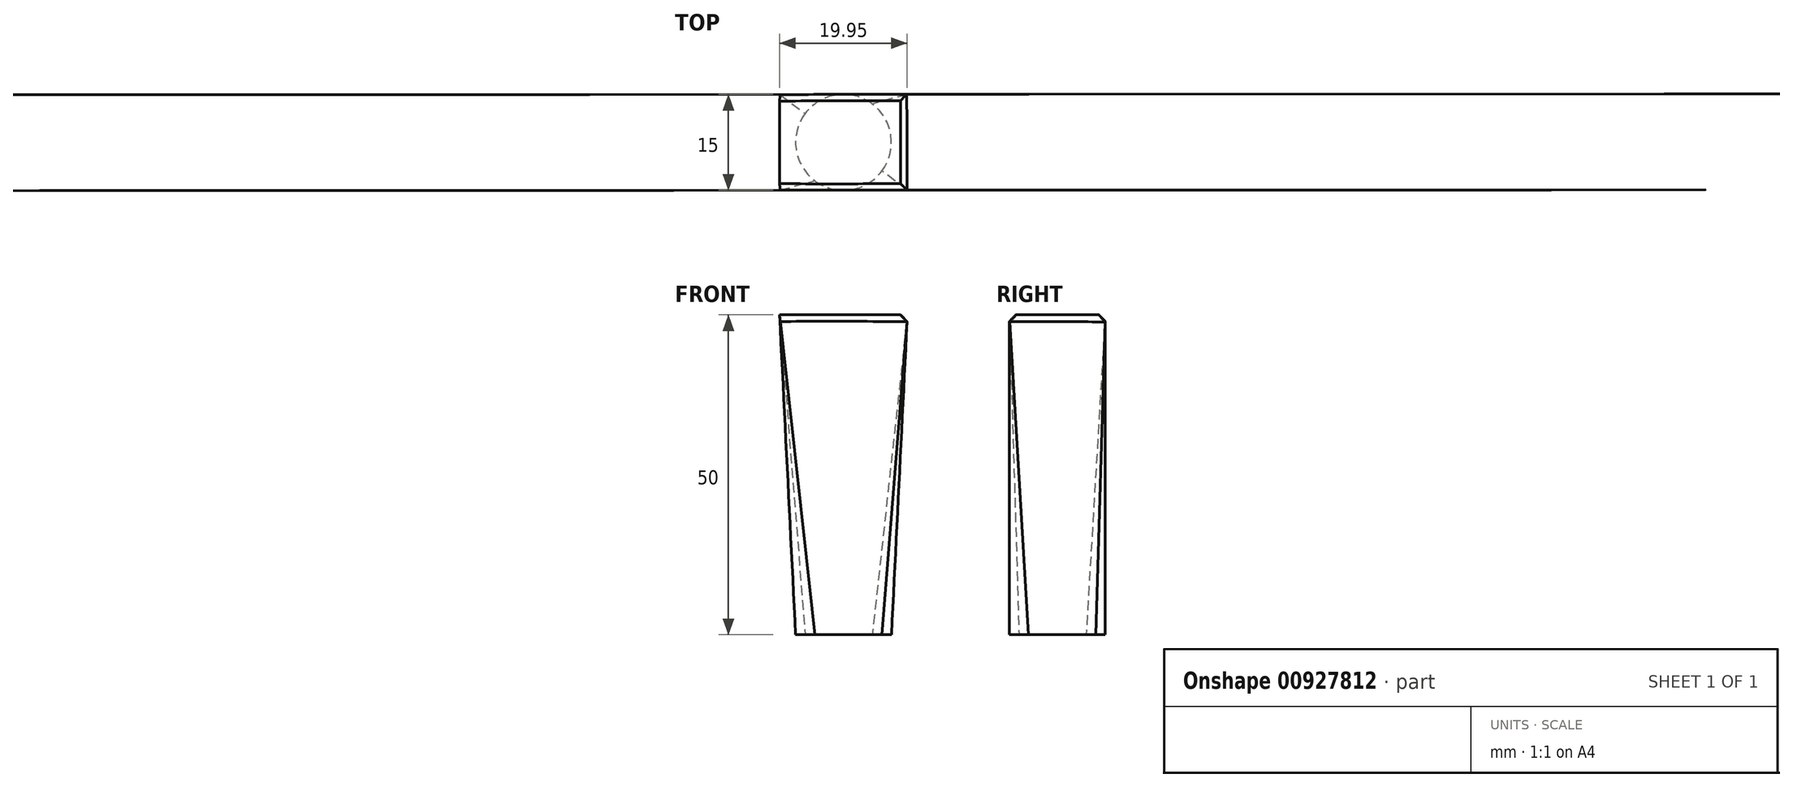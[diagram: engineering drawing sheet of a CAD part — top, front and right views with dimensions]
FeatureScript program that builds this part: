
annotation { "Feature Type Name" : "Feature", "Feature Type Description" : "" }
export const myFeature = defineFeature(function(context is Context, id is Id, definition is map)
    precondition{}
    {
        {
            var Q0;
            Q0=qCreatedBy(makeId("Top.planeOp"),FACE);
            var sketch = newSketch(context, id + "F0", { "sketchPlane" : qUnion([Q0])});
            skCircle(sketch, "E0", {"center": v(0, 0) * mm, "radius": 7.5 * mm});
            skSolve(sketch);
        }
        {
            var Q0;
            Q0=qCreatedBy(makeId("Top.planeOp"),FACE);
            cPlane(context, id + "F1", {"entities" : qUnion([Q0]), "cplaneType" : CPlaneType.OFFSET, "offset" : 50 * mm, "width" : 150 * mm, "height" : 150 * mm});
        }
        {
            var Q0;
            Q0=qCreatedBy(id+"F1.planeOp",FACE);
            var sketch = newSketch(context, id + "F2", { "sketchPlane" : qUnion([Q0])});
            skLineSegment(sketch, "E1.bottom", {"start": v(-10, 7.5) * mm, "end": v(10, 7.5) * mm});
            skLineSegment(sketch, "E1.top", {"start": v(-10, -7.5) * mm, "end": v(10, -7.5) * mm});
            skLineSegment(sketch, "E1.left", {"start": v(-10, 7.5) * mm, "end": v(-10, -7.5) * mm});
            skLineSegment(sketch, "E1.right", {"start": v(10, 7.5) * mm, "end": v(10, -7.5) * mm});
            skPoint(sketch, "E1.middle", {"position": v(0, 0) * mm});
            skSolve(sketch);
        }
        {
            var Q0;
            Q0=makeQuery(id+"F2.imprint","IMPRINT",FACE,{"disambiguationData":[TD([[makeQuery(id+"F2.imprint","IMPRINT",EDGE,{"derivedFrom":sQuery(id+"F2.wireOp",EDGE,"E1.bottom")}),-1.0]])]});
            var Q1;
            Q1=makeQuery(id+"F0.imprint","IMPRINT",FACE,{"disambiguationData":[TD([[makeQuery(id+"F0.imprint","IMPRINT",EDGE,{"derivedFrom":sQuery(id+"F0.wireOp",EDGE,"E0")}),1.0]])]});
            loft(context, id + "F3", {"sheetProfilesArray" : [{ "sheetProfileEntities" : qUnion([Q0]) }, { "sheetProfileEntities" : qUnion([Q1]) }]});
        }
        {
            var Q0;
            Q0=makeQuery(id+"F3.opLoft","MID_CAP_EDGE",EDGE,{"disambiguationData":[OSD([sQuery(id+"F2.wireOp",EDGE,"E1.top"),sQuery(id+"F2.wireOp",EDGE,"E1.left"),sQuery(id+"F2.wireOp",EDGE,"E1.right")])],"capPos":0.0});
            var Q1;
            Q1=makeQuery(id+"F3.opLoft","MID_CAP_EDGE",EDGE,{"disambiguationData":[OSD([sQuery(id+"F2.wireOp",EDGE,"E1.bottom"),sQuery(id+"F2.wireOp",EDGE,"E1.top"),sQuery(id+"F2.wireOp",EDGE,"E1.right")])],"capPos":0.0});
            var Q2;
            Q2=makeQuery(id+"F3.opLoft","MID_CAP_EDGE",EDGE,{"disambiguationData":[OSD([sQuery(id+"F2.wireOp",EDGE,"E1.bottom"),sQuery(id+"F2.wireOp",EDGE,"E1.left"),sQuery(id+"F2.wireOp",EDGE,"E1.right")])],"capPos":0.0});
            chamfer(context, id + "F4", {"entities" : qUnion([Q0, Q1, Q2]), "width" : 1 * mm, "tangentPropagation" : true});
        }
    });
